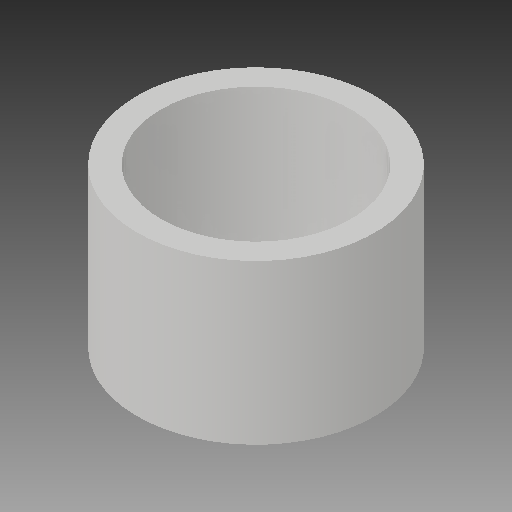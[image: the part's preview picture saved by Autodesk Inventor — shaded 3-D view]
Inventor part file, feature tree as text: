
AUTODESK INVENTOR PART (.ipt)
format: ipt  version: 2018.2 (Build 222227000, 227)  size: 101,888 bytes
history: native  units: mm
features: other x1, extrude x1, sketch x1
ambient origin geometry x8: Origin, YZ Plane, XZ Plane, XY Plane, X Axis, Y Axis, Z Axis, Center Point
bodies: Body1 (feature_tree)
feature tree (3):
  other  "ソリッド1"
  extrude  "押し出し1"  Depth=10.0mm
  sketch  "スケッチ1"
